# Revit family: QF_LAINOX_Oracle XS--
name_source: partatom
category: Specialty Equipment
units: mm (PartAtom-declared; Revit-internal decimal feet)

## family parameters
Always vertical = Yes
Cut with Voids When Loaded = No
OmniClass Number = 23.40.40.14
OmniClass Title = Food Service Equipment
Part Type = Normal
Room Calculation Point = No
Round Connector Dimension = Use Diameter
Shared = No
Work Plane-Based = No

## types (3) — shared parameters
1 Description_ENG = HIGH SPEED OVEN
2 Description_USA = HIGH SPEED OVEN
3 Description_ESP = HORNO DE ALTA VELOCIDAD
4 Description_POR = FORNO DE COZIMENTO ACELERADO
5 Description_FRA = FOUR À GRANDE VITESSE
6 Description_DEU = HOCHGESCHWINDIGKEITSOFEN
7 Description_ITA = FORNO COTTURA ACCELERATA
Accessory = No
CE Approved = Yes
Clearance_Rear = 50 mm  [stored 0.164042 ft]
Clearance_Side_LH = 50 mm  [stored 0.164042 ft]
Clearance_Side_RH = 50 mm  [stored 0.164042 ft]
Clearance_Upper = 500 mm  [stored 1.64042 ft]
Conn Plug = Plug IEC309
Cycle = 50 Hz
D2 = 2 mm  [stored 0.00656168 ft]
D5 = 5 mm  [stored 0.0164042 ft]
Depth Actual = 624 mm  [stored 2.04724 ft]
Description = HIGH SPEED OVEN
Elec Connection Height = 32 mm  [stored 0.104987 ft]
Electric power = 3600 W
Electrical Remarks = Power Cable 2 mt
FL Amps = 16 A
Foodservice Equipment Identifier = Yes
Height Actual = 579 mm  [stored 1.89961 ft]
Identify Quantity as Lot = No
Keynote = 0
Language ID = 1
Language_Check = 1
Legs Height = 80 mm  [stored 0.262467 ft]
Length Actual = 356 mm  [stored 1.16798 ft]
Main switch integrated = No
Manufacturer = LAINOX
Mat_Case = QF_Stainless-Brushed
Mat_Clearance = QF_Clearance
Mat_LCD = QF_Glass-Cast-Clear
Mat_Logo = QF_Plastic-White-Matte
Mat_Logo_a = QF_Plastic-Gray-Matte
Mat_Plastic_Black Glossy = QF_Plastic-Black-Glossy
Mat_Plastic_Black Matte = QF_Plastic-Black-Matte
Number of Poles = 1
Phase = 1
Potential Equalisation = Yes
URL Manufacturer = https://www.lainox.com
Volt Free Conn = No
Volts = 230 V
Weight = 50.00 kg
zero-valued in all types: Base, Default Elevation

## per-type parameters (varying)
| type | Item Number | Mat_Case_Paint | Model | URL Cutsheet |
| ORXSTR_Red_230V 1Ph 50Hz | ORXSTR | QF_Plastic-Red | ORXSTR Red | ORXSTR.pdf |
| ORXSTG_Steel_230V 1Ph 50Hz | ORXSTG | QF_Stainless-Brushed | ORXSTG Steel | ORXSTG.pdf |
| ORXSTB_Black_230V 1Ph 50Hz | ORXSTB | QF_Plastic-Black-Matte | ORXSTB Black | ORXSTB.pdf |

note: [stored X ft] marks values corroborated as IEEE doubles in the binary element streams (Revit-internal decimal feet)

## geometry (parser evidence)
native form markers: Sweep x22
no freeform markers — native parametric forms only
